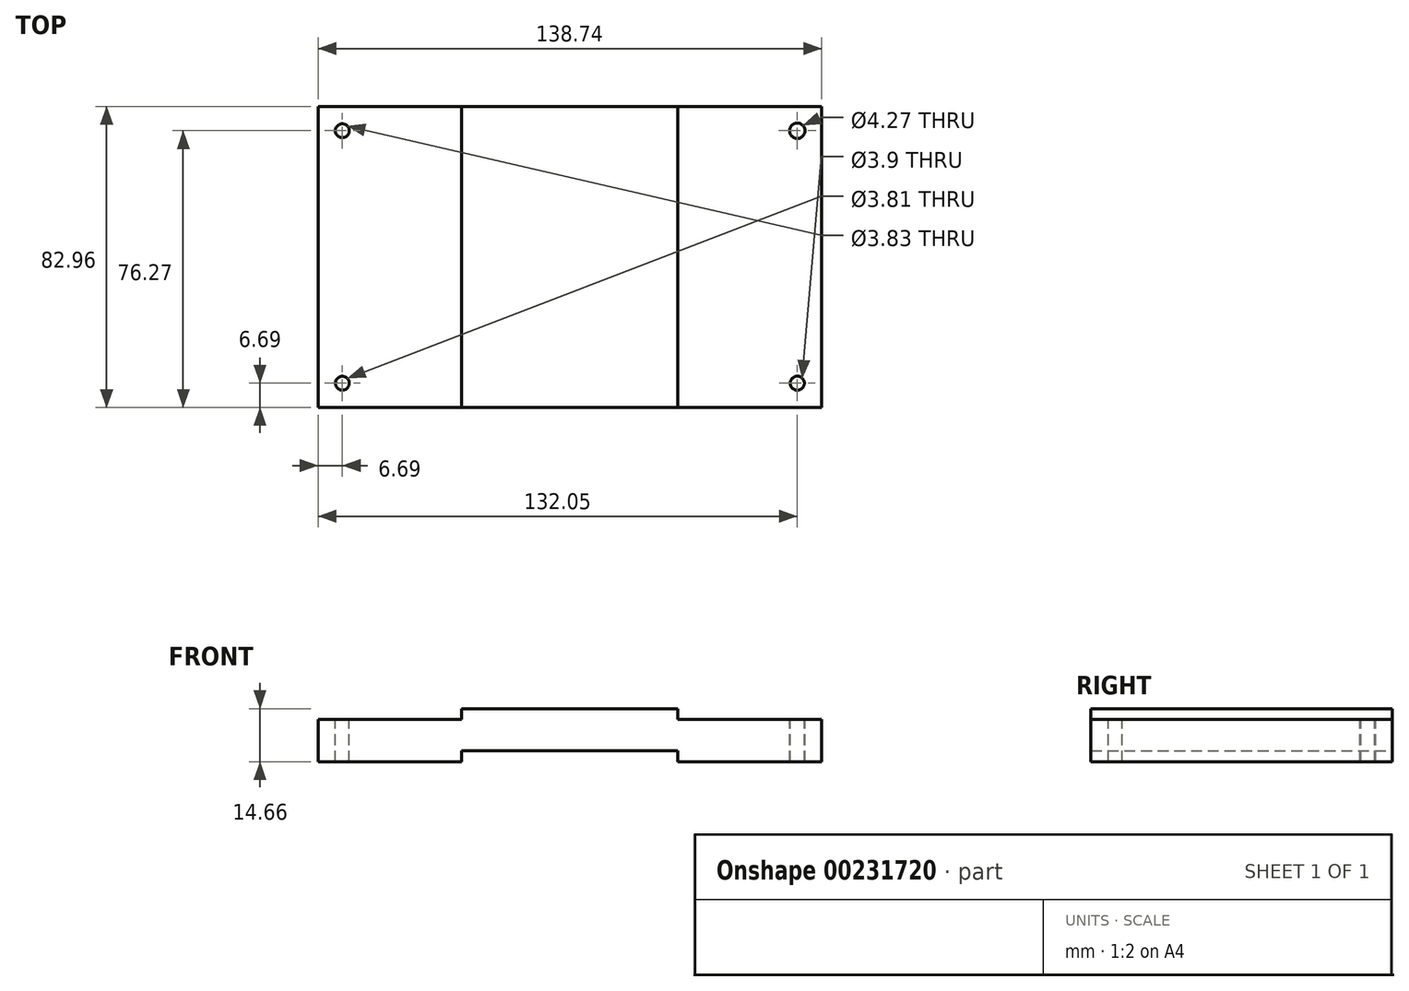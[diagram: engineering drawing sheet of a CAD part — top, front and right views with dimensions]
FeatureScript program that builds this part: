
annotation { "Feature Type Name" : "Feature", "Feature Type Description" : "" }
export const myFeature = defineFeature(function(context is Context, id is Id, definition is map)
    precondition{}
    {
        {
            var Q0;
            Q0=qCreatedBy(makeId("Front.planeOp"),FACE);
            var sketch = newSketch(context, id + "F0", { "sketchPlane" : qUnion([Q0])});
            skLineSegment(sketch, "E0.bottom", {"start": v(29.77, 5.8) * mm, "end": v(-29.77, 5.8) * mm});
            skLineSegment(sketch, "E0.top", {"start": v(29.77, -5.81) * mm, "end": v(-29.77, -5.81) * mm});
            skLineSegment(sketch, "E0.left", {"start": v(29.77, 5.8) * mm, "end": v(29.77, 2.8) * mm});
            skLineSegment(sketch, "E0.right", {"start": v(-29.77, 5.8) * mm, "end": v(-29.77, 2.8) * mm});
            skPoint(sketch, "E0.middle", {"position": v(0, 0) * mm});
            skLineSegment(sketch, "E1.bottom", {"start": v(-29.77, 2.8) * mm, "end": v(-69.37, 2.8) * mm});
            skLineSegment(sketch, "E1.top", {"start": v(-29.77, -8.85) * mm, "end": v(-69.37, -8.85) * mm});
            skLineSegment(sketch, "E1.left", {"start": v(-29.77, -5.81) * mm, "end": v(-29.77, -8.85) * mm});
            skLineSegment(sketch, "E1.right", {"start": v(-69.37, 2.8) * mm, "end": v(-69.37, -8.85) * mm});
            skLineSegment(sketch, "E2.bottom", {"start": v(29.77, 2.8) * mm, "end": v(69.37, 2.8) * mm});
            skLineSegment(sketch, "E2.top", {"start": v(29.77, -8.85) * mm, "end": v(69.37, -8.85) * mm});
            skLineSegment(sketch, "E2.left", {"start": v(29.77, -5.81) * mm, "end": v(29.77, -8.85) * mm});
            skLineSegment(sketch, "E2.right", {"start": v(69.37, 2.8) * mm, "end": v(69.37, -8.85) * mm});
            skSolve(sketch);
        }
        {
            var Q0;
            Q0=makeQuery(id+"F0.imprint","IMPRINT",FACE,{"disambiguationData":[TD([[makeQuery(id+"F0.imprint","IMPRINT",EDGE,{"derivedFrom":sQuery(id+"F0.wireOp",EDGE,"E0.bottom")}),1.0]])]});
            extrude(context, id + "F1", {"entities" : qUnion([Q0]), "endBound" : BoundingType.SYMMETRIC, "depth" : 82.96 * mm});
        }
        {
            var Q0;
            Q0=qCreatedBy(makeId("Top.planeOp"),FACE);
            cPlane(context, id + "F2", {"entities" : qUnion([Q0]), "cplaneType" : CPlaneType.OFFSET, "offset" : 6.1 * mm, "width" : 152.4 * mm, "height" : 152.4 * mm});
        }
        {
            var Q0;
            Q0=qCreatedBy(id+"F2.planeOp",FACE);
            var sketch = newSketch(context, id + "F3", { "sketchPlane" : qUnion([Q0])});
            skCircle(sketch, "E3", {"center": v(-62.68, 34.79) * mm, "radius": 1.92 * mm});
            skCircle(sketch, "E4", {"center": v(-62.68, -34.79) * mm, "radius": 1.9 * mm});
            skCircle(sketch, "E5", {"center": v(62.68, 34.79) * mm, "radius": 2.14 * mm});
            skCircle(sketch, "E6", {"center": v(62.68, -34.79) * mm, "radius": 1.95 * mm});
            skSolve(sketch);
        }
        {
            var Q0;
            Q0=makeQuery(id+"F3.imprint","IMPRINT",FACE,{"disambiguationData":[TD([[makeQuery(id+"F3.imprint","IMPRINT",EDGE,{"derivedFrom":sQuery(id+"F3.wireOp",EDGE,"E4")}),1.0]])]});
            var Q1;
            Q1=makeQuery(id+"F3.imprint","IMPRINT",FACE,{"disambiguationData":[TD([[makeQuery(id+"F3.imprint","IMPRINT",EDGE,{"derivedFrom":sQuery(id+"F3.wireOp",EDGE,"E3")}),1.0]])]});
            var Q2;
            Q2=makeQuery(id+"F3.imprint","IMPRINT",FACE,{"disambiguationData":[TD([[makeQuery(id+"F3.imprint","IMPRINT",EDGE,{"derivedFrom":sQuery(id+"F3.wireOp",EDGE,"E5")}),1.0]])]});
            var Q3;
            Q3=makeQuery(id+"F3.imprint","IMPRINT",FACE,{"disambiguationData":[TD([[makeQuery(id+"F3.imprint","IMPRINT",EDGE,{"derivedFrom":sQuery(id+"F3.wireOp",EDGE,"E6")}),1.0]])]});
            extrude(context, id + "F4", {"entities" : qUnion([Q0, Q1, Q2, Q3]), "operationType" : NewBodyOperationType.REMOVE, "endBound" : BoundingType.THROUGH_ALL, "oppositeDirection" : true, "depth" : 25.4 * mm});
        }
    });
